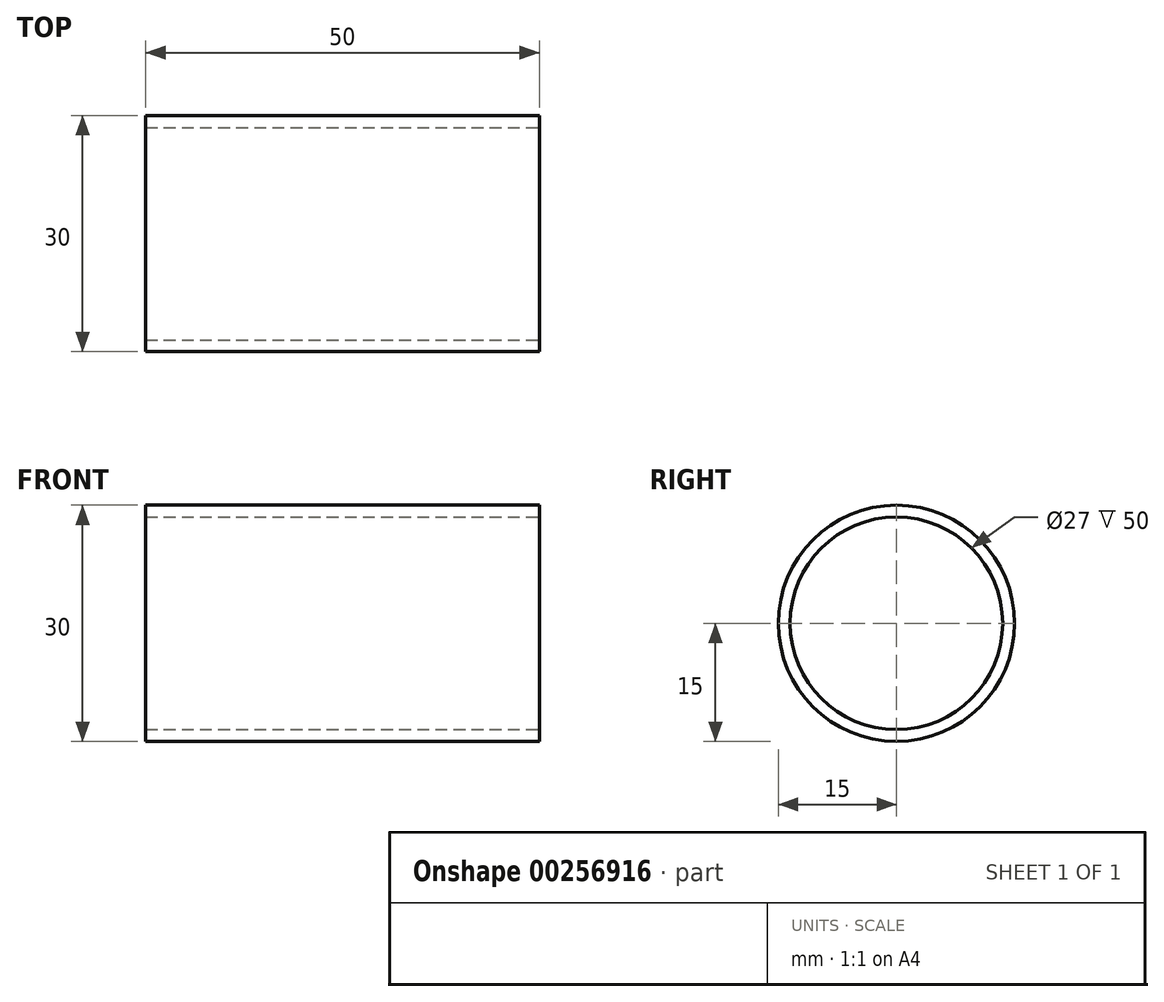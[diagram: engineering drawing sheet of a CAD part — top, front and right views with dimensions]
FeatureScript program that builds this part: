
annotation { "Feature Type Name" : "Feature", "Feature Type Description" : "" }
export const myFeature = defineFeature(function(context is Context, id is Id, definition is map)
    precondition{}
    {
        {
            var Q0;
            Q0=qCreatedBy(makeId("Right.planeOp"),FACE);
            var sketch = newSketch(context, id + "F0", { "sketchPlane" : qUnion([Q0])});
            skCircle(sketch, "E0", {"center": v(0, 0) * mm, "radius": 13.5 * mm});
            skCircle(sketch, "E1", {"center": v(0, 0) * mm, "radius": 15 * mm});
            skSolve(sketch);
        }
        {
            var Q0;
            Q0=makeQuery(id+"F0.imprint","IMPRINT",FACE,{"disambiguationData":[TD([[makeQuery(id+"F0.imprint","IMPRINT",EDGE,{"derivedFrom":sQuery(id+"F0.wireOp",EDGE,"E0")}),-1.0]])]});
            extrude(context, id + "F1", {"entities" : qUnion([Q0]), "oppositeDirection" : true, "depth" : 50 * mm});
        }
    });
